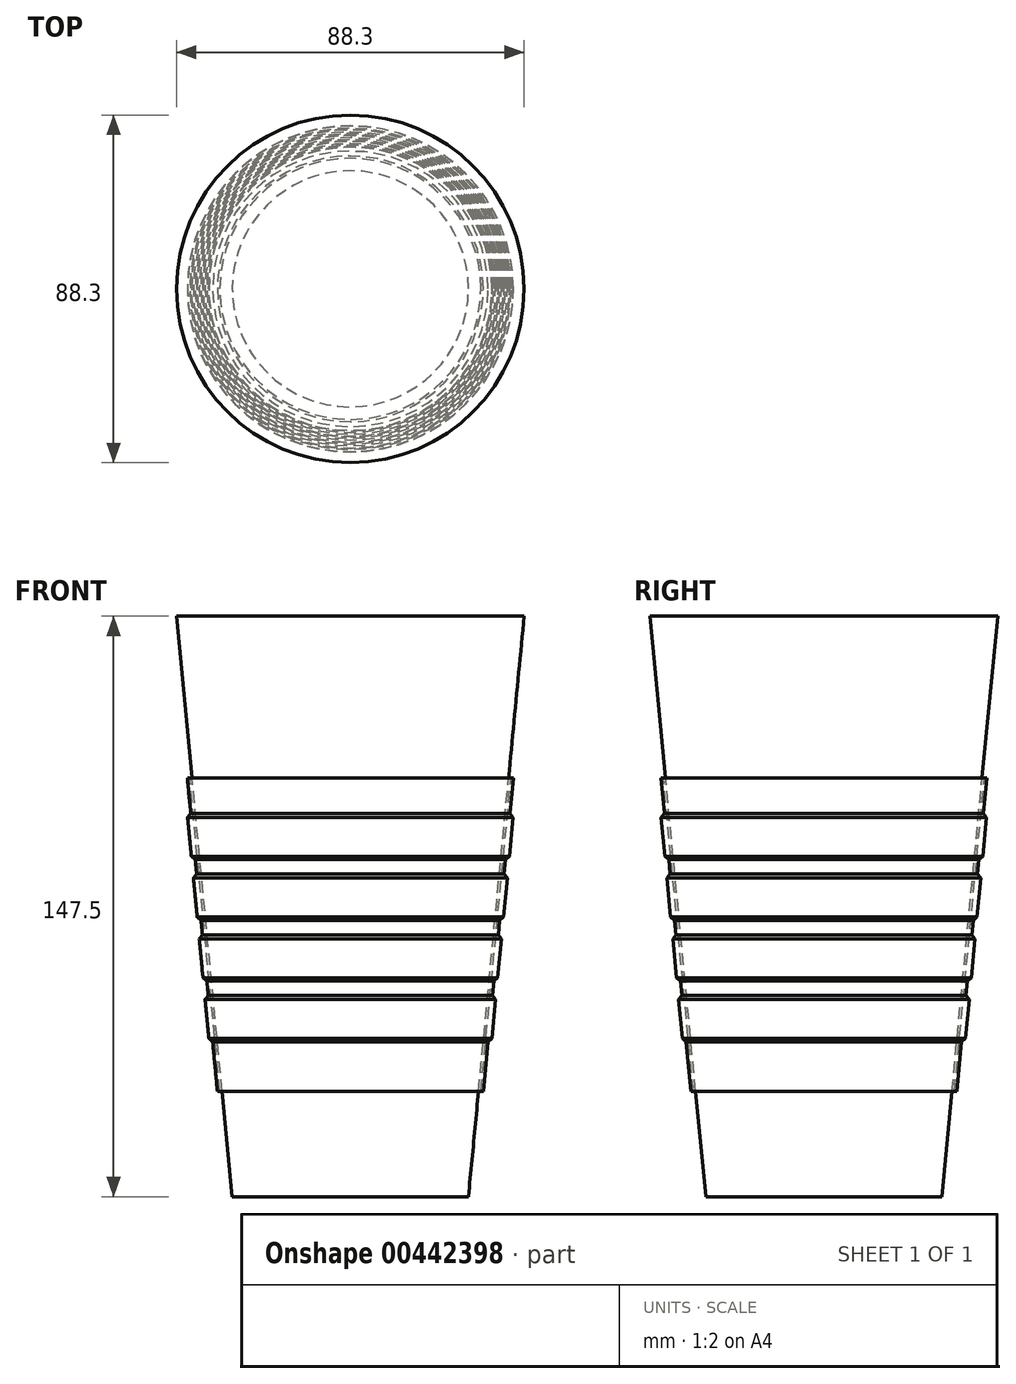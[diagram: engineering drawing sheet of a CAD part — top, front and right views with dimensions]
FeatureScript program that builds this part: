
annotation { "Feature Type Name" : "Feature", "Feature Type Description" : "" }
export const myFeature = defineFeature(function(context is Context, id is Id, definition is map)
    precondition{}
    {
        {
            var Q0;
            Q0=qCreatedBy(makeId("Top.planeOp"),FACE);
            var sketch = newSketch(context, id + "F0", { "sketchPlane" : qUnion([Q0])});
            skCircle(sketch, "E0", {"center": v(0, 0) * mm, "radius": 30 * mm});
            skSolve(sketch);
        }
        {
            var Q0;
            Q0=qCreatedBy(makeId("Top.planeOp"),FACE);
            cPlane(context, id + "F1", {"entities" : qUnion([Q0]), "cplaneType" : CPlaneType.OFFSET, "offset" : 147.5 * mm, "width" : 150 * mm, "height" : 150 * mm});
        }
        {
            var Q0;
            Q0=qCreatedBy(id+"F1.planeOp",FACE);
            var sketch = newSketch(context, id + "F2", { "sketchPlane" : qUnion([Q0])});
            skCircle(sketch, "E1", {"center": v(0, 0) * mm, "radius": 44.15 * mm});
            skSolve(sketch);
        }
        {
            var Q0;
            Q0=makeQuery(id+"F0.imprint","IMPRINT",FACE,{"disambiguationData":[TD([[makeQuery(id+"F0.imprint","IMPRINT",EDGE,{"derivedFrom":sQuery(id+"F0.wireOp",EDGE,"E0")}),1.0]])]});
            var Q1;
            Q1=makeQuery(id+"F2.imprint","IMPRINT",FACE,{"disambiguationData":[TD([[makeQuery(id+"F2.imprint","IMPRINT",EDGE,{"derivedFrom":sQuery(id+"F2.wireOp",EDGE,"E1")}),1.0]])]});
            loft(context, id + "F3", {"sheetProfilesArray" : [{ "sheetProfileEntities" : qUnion([Q0]) }, { "sheetProfileEntities" : qUnion([Q1]) }]});
        }
        {
            var Q0;
            Q0=qCreatedBy(makeId("Front.planeOp"),FACE);
            var sketch = newSketch(context, id + "F4", { "sketchPlane" : qUnion([Q0])});
            skLineSegment(sketch, "E2", {"start": v(44.15, 147.5) * mm, "end": v(30, 0) * mm, "construction": true});
            skLineSegment(sketch, "E3", {"start": v(-30, 0) * mm, "end": v(-44.15, 147.5) * mm, "construction": true});
            skLineSegment(sketch, "E4", {"start": v(0, 0) * mm, "end": v(0, 147.5) * mm, "construction": true});
            skLineSegment(sketch, "E5", {"start": v(-40.21, 106.44) * mm, "end": v(-40.81, 106.44) * mm, "construction": true});
            skLineSegment(sketch, "E6", {"start": v(-40.81, 106.44) * mm, "end": v(-33.18, 26.86) * mm});
            skLineSegment(sketch, "E7", {"start": v(-33.18, 26.86) * mm, "end": v(-33.77, 26.8) * mm});
            skLineSegment(sketch, "E8", {"start": v(-33.77, 26.8) * mm, "end": v(-41.41, 106.44) * mm});
            skLineSegment(sketch, "E9", {"start": v(-41.41, 106.44) * mm, "end": v(-40.81, 106.44) * mm});
            skLineSegment(sketch, "E10", {"start": v(-41.41, 106.44) * mm, "end": v(-40.46, 96.48) * mm, "construction": true});
            skLineSegment(sketch, "E11", {"start": v(-40.46, 96.48) * mm, "end": v(-41.35, 96.4) * mm, "construction": true});
            skLineSegment(sketch, "E12", {"start": v(-41.35, 96.4) * mm, "end": v(-40.4, 86.44) * mm});
            skLineSegment(sketch, "E13", {"start": v(-40.4, 86.44) * mm, "end": v(-39.41, 85.63) * mm});
            skLineSegment(sketch, "E14", {"start": v(-41.35, 96.4) * mm, "end": v(-40.54, 97.38) * mm});
            skLineSegment(sketch, "E15.1.0.0", {"start": v(-39.87, 80.97) * mm, "end": v(-39.06, 81.95) * mm});
            skLineSegment(sketch, "E15.1.0.1", {"start": v(-39.87, 80.97) * mm, "end": v(-38.92, 71.01) * mm});
            skLineSegment(sketch, "E15.1.0.2", {"start": v(-38.92, 71.01) * mm, "end": v(-37.93, 70.2) * mm});
            skLineSegment(sketch, "E15.2.0.0", {"start": v(-38.4, 65.54) * mm, "end": v(-37.58, 66.52) * mm});
            skLineSegment(sketch, "E15.2.0.1", {"start": v(-38.4, 65.54) * mm, "end": v(-37.44, 55.58) * mm});
            skLineSegment(sketch, "E15.2.0.2", {"start": v(-37.44, 55.58) * mm, "end": v(-36.45, 54.77) * mm});
            skLineSegment(sketch, "E15.3.0.0", {"start": v(-36.91, 50.1) * mm, "end": v(-36.1, 51.09) * mm});
            skLineSegment(sketch, "E15.3.0.1", {"start": v(-36.91, 50.1) * mm, "end": v(-35.96, 40.15) * mm});
            skLineSegment(sketch, "E15.3.0.2", {"start": v(-35.96, 40.15) * mm, "end": v(-34.97, 39.34) * mm});
            skLineSegment(sketch, "E15.direction1", {"start": v(-41.35, 96.4) * mm, "end": v(-39.87, 80.97) * mm, "construction": true});
            skSolve(sketch);
        }
        {
            var Q0;
            Q0=makeQuery(id+"F4.imprint","IMPRINT",FACE,{"disambiguationData":[TD([[makeQuery(id+"F4.imprint","IMPRINT",EDGE,{"derivedFrom":sQuery(id+"F4.wireOp",EDGE,"E12")}),1.0]])]});
            var Q1;
            Q1=makeQuery(id+"F4.imprint","IMPRINT",FACE,{"disambiguationData":[TD([[makeQuery(id+"F4.imprint","IMPRINT",EDGE,{"derivedFrom":sQuery(id+"F4.wireOp",EDGE,"E6")}),-1.0]])]});
            var Q2;
            {var subQ0=sQuery(id+"F4.wireOp",EDGE,"E15.1.0.0");Q2=makeQuery(id+"F4.imprint","IMPRINT",FACE,{"disambiguationData":[TD([[makeQuery(id+"F4.imprint","IMPRINT",EDGE,{"derivedFrom":subQ0}),-1.0]])]});}
            var Q3;
            {var subQ0=sQuery(id+"F4.wireOp",EDGE,"E15.3.0.0");Q3=makeQuery(id+"F4.imprint","IMPRINT",FACE,{"disambiguationData":[TD([[makeQuery(id+"F4.imprint","IMPRINT",EDGE,{"derivedFrom":subQ0}),-1.0]])]});}
            var Q4;
            {var subQ0=sQuery(id+"F4.wireOp",EDGE,"E15.2.0.0");Q4=makeQuery(id+"F4.imprint","IMPRINT",FACE,{"disambiguationData":[TD([[makeQuery(id+"F4.imprint","IMPRINT",EDGE,{"derivedFrom":subQ0}),-1.0]])]});}
            var Q5;
            Q5=sQuery(id+"F4.wireOp",EDGE,"E4");
            revolve(context, id + "F5", {"entities" : qUnion([Q0, Q1, Q2, Q3, Q4]), "axis" : qUnion([Q5]), "revolveType" : RevolveType.FULL});
        }
    });
